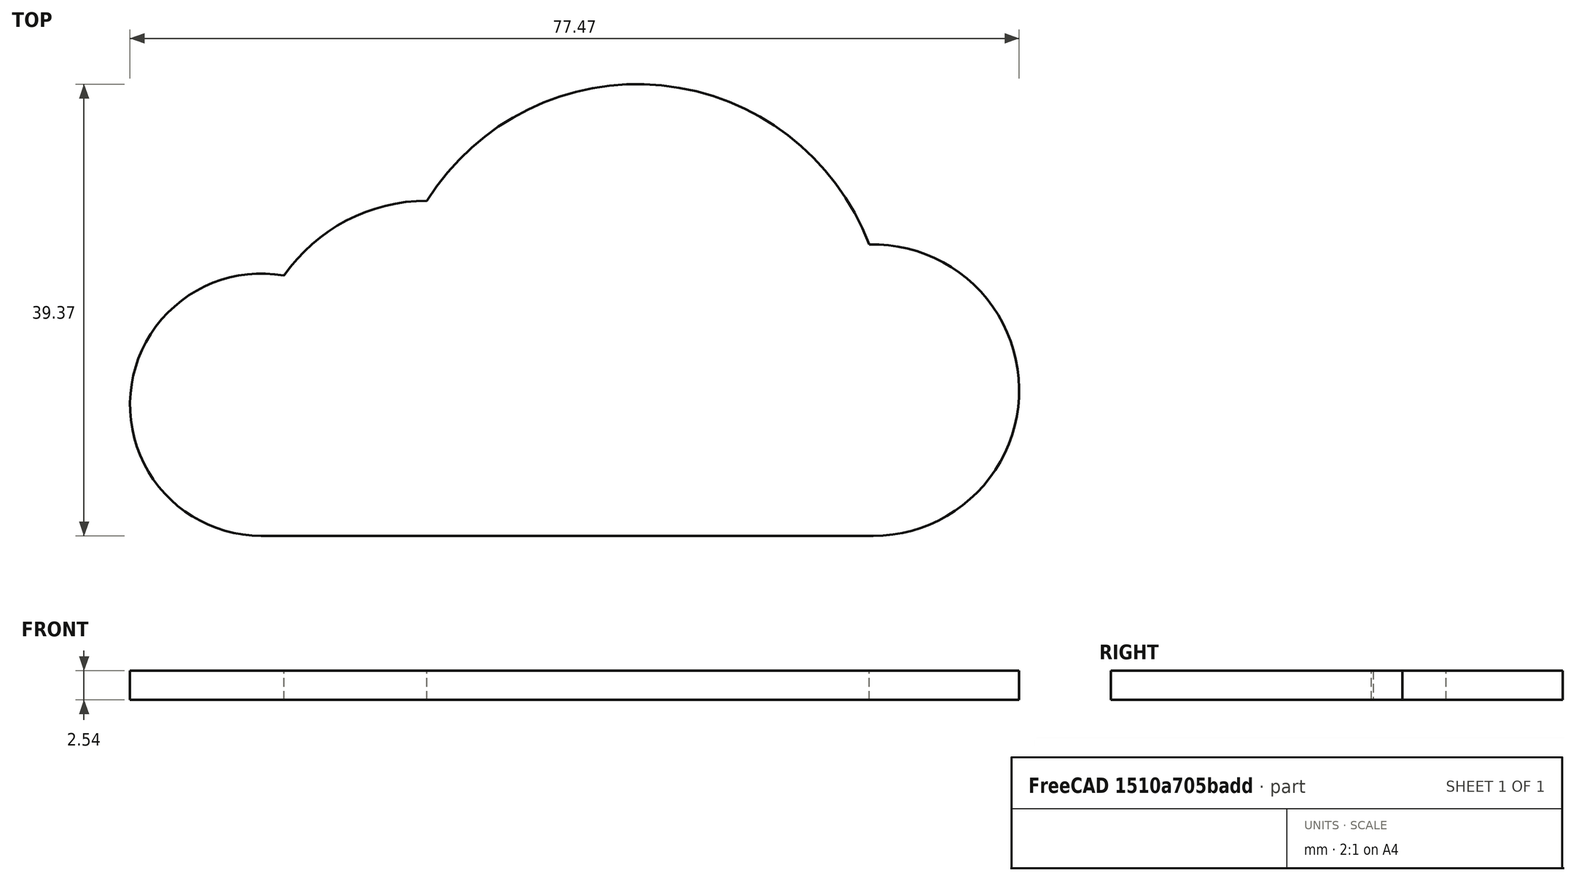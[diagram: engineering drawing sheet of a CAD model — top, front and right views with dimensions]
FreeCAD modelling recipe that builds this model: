
FCSTD DOCUMENT  (FreeCAD 0.16R6712 (Git))
Label: steam_badge3
License: All rights reserved
LicenseURL: http://en.wikipedia.org/wiki/All_rights_reserved
objects: Sketcher::SketchObject×1, PartDesign::Pad×1
note: 3 computed .brp shape members not serialized (recipe doc carries the construction recipe); baked Part::Feature solids carry a one-line shape summary decoded from their .brp

FEATURE [Sketcher::SketchObject] Sketch
  sketch-geometry (11):
    g0: LineSegment [constr] StartX=0 StartY=0 StartZ=0 EndX=28.702 EndY=0 EndZ=0
    g1: LineSegment [constr] StartX=28.702 StartY=0 StartZ=0 EndX=28.702 EndY=38.1 EndZ=0
    g2: ArcOfCircle CenterX=28.702 CenterY=49.53 CenterZ=0 NormalX=0 NormalY=0 NormalZ=1 Radius=11.43 StartAngle=1.39691 EndAngle=4.71239
    g3: LineSegment StartX=28.702 StartY=38.1 StartZ=0 EndX=82.042 EndY=38.1 EndZ=0
    g4: ArcOfCircle CenterX=82.042 CenterY=50.8 CenterZ=0 NormalX=0 NormalY=0 NormalZ=1 Radius=12.7 StartAngle=4.71239 EndAngle=7.88323
    g5: ArcOfCircle CenterX=43.18 CenterY=52.07 CenterZ=0 NormalX=0 NormalY=0 NormalZ=1 Radius=15.24 StartAngle=1.57265 EndAngle=2.53262
    g6: LineSegment [constr] StartX=43.18 StartY=52.07 StartZ=0 EndX=61.468 EndY=52.07 EndZ=0
    g7: LineSegment [constr] StartX=61.468 StartY=52.07 StartZ=0 EndX=61.468 EndY=55.88 EndZ=0
    g8: ArcOfCircle CenterX=61.468 CenterY=55.88 CenterZ=0 NormalX=0 NormalY=0 NormalZ=1 Radius=21.59 StartAngle=0.360444 EndAngle=2.58369
    g9: LineSegment [constr] StartX=28.702 StartY=49.53 StartZ=0 EndX=43.18 EndY=49.53 EndZ=0
    g10: LineSegment [constr] StartX=43.18 StartY=49.53 StartZ=0 EndX=43.18 EndY=52.07 EndZ=0
  constraints (34):
    c: Coincident(g-1,g0)
    c: PointOnObject(g0,g-1)
    c: Vertical(g1)
    c: DistanceX(g0,g0) = 28.702
    c: DistanceY(g1,g2) = 49.53
    c: Radius(g2) = 11.43
    c: Horizontal(g3)
    c: DistanceX(g3,g3) = 53.34
    c: DistanceX(g2,g3) = 0
    c: DistanceX(g4,g3) = 0
    c: Radius(g4) = 12.7
    c: Coincident(g0,g1)
    c: Radius(g5) = 15.24
    c: Horizontal(g6)
    c: Vertical(g7)
    c: DistanceX(g6,g6) = 18.288
    c: Coincident(g6,g7)
    c: Radius(g8) = 21.59
    c: Horizontal(g9)
    c: Coincident(g2,g9)
    c: DistanceX(g9,g9) = 14.478
    c: Vertical(g10)
    c: Coincident(g9,g10)
    c: DistanceY(g10,g10) = 2.54
    c: Coincident(g2,g5)
    c: Coincident(g2,g1)
    c: Coincident(g1,g3)
    c: Coincident(g3,g4)
    c: Coincident(g10,g5)
    c: Coincident(g6,g5)
    c: DistanceY(g7,g7) = 3.81
    c: Coincident(g7,g8)
    c: Coincident(g8,g5)
    c: Coincident(g4,g8)
FEATURE [PartDesign::Pad] Pad
  Length = 2.54
  Length2 = 100
  Sketch = -> Sketch
  Type = 0
